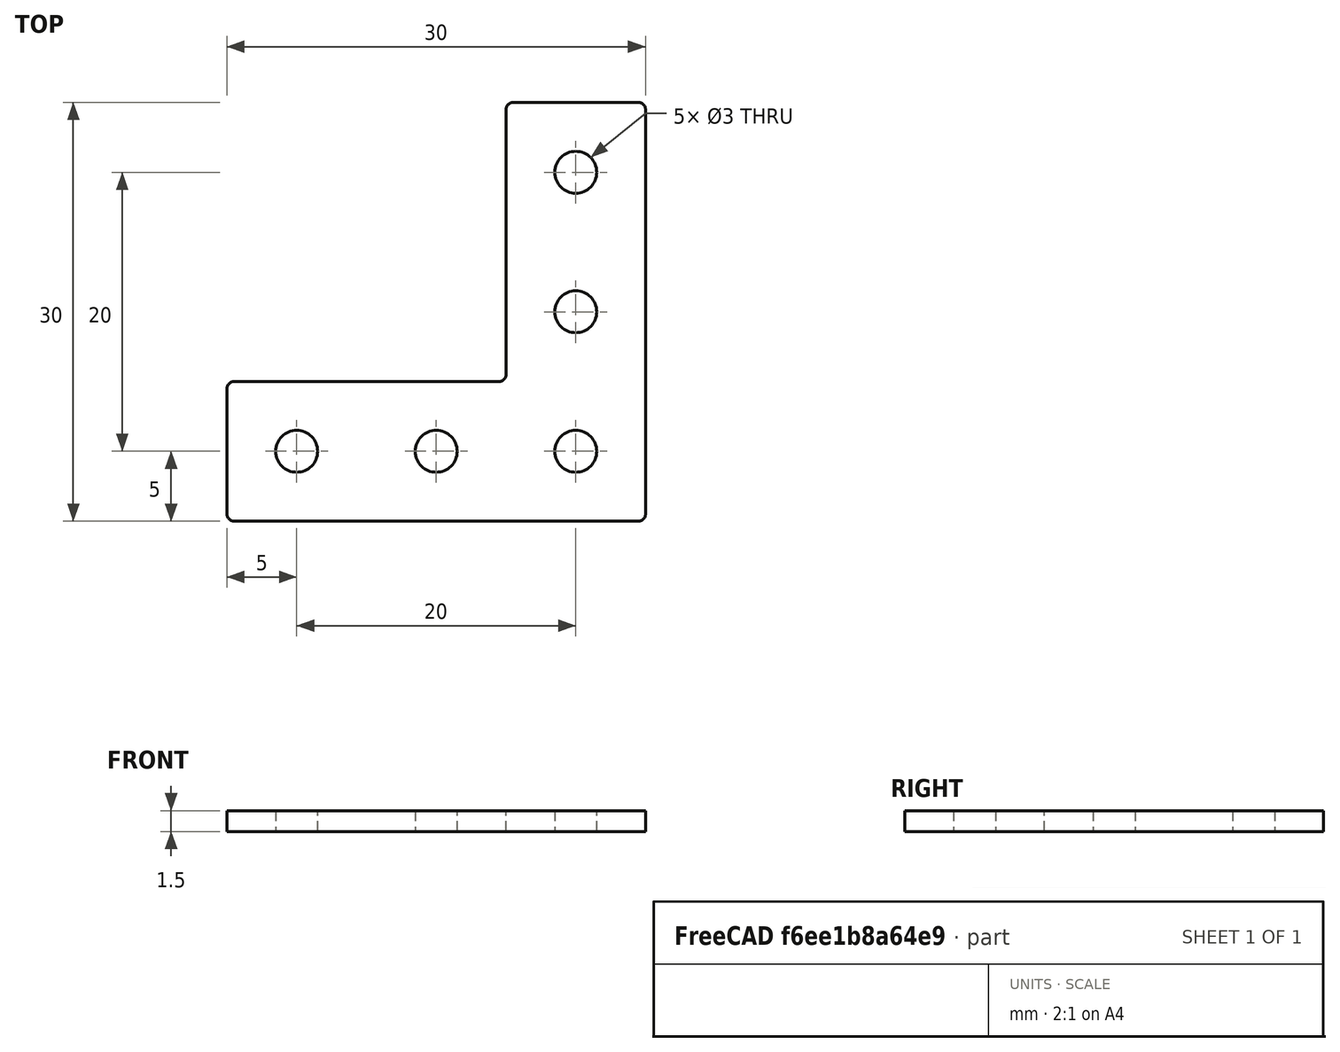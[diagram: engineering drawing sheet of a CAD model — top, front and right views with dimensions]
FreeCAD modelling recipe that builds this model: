
FCSTD DOCUMENT  (FreeCAD 0.18R16146 (Git))
Label: makerbeam_bracket_rightangle
License: All rights reserved
LicenseURL: http://en.wikipedia.org/wiki/All_rights_reserved
objects: Sketcher::SketchObject×1, PartDesign::Pad×1, PartDesign::Fillet×1, PartDesign::Body×1
note: 5 computed .brp shape members not serialized (recipe doc carries the construction recipe); baked Part::Feature solids carry a one-line shape summary decoded from their .brp

FEATURE [Sketcher::SketchObject] Sketch
  MapMode = 5
  Support = -> [XY_Plane]
  sketch-geometry (11):
    g0: Circle CenterX=-20 CenterY=0 CenterZ=0 NormalX=0 NormalY=0 NormalZ=1 AngleXU=0 Radius=1.5
    g1: Circle CenterX=-10 CenterY=0 CenterZ=0 NormalX=0 NormalY=0 NormalZ=1 AngleXU=0 Radius=1.5
    g2: Circle CenterX=0 CenterY=0 CenterZ=0 NormalX=0 NormalY=0 NormalZ=1 AngleXU=0 Radius=1.5
    g3: Circle CenterX=0 CenterY=10 CenterZ=0 NormalX=0 NormalY=0 NormalZ=1 AngleXU=0 Radius=1.5
    g4: LineSegment StartX=-25 StartY=-5 StartZ=0 EndX=5 EndY=-5 EndZ=0
    g5: LineSegment StartX=5 StartY=-5 StartZ=0 EndX=5 EndY=25 EndZ=0
    g6: LineSegment StartX=5 StartY=25 StartZ=0 EndX=-5 EndY=25 EndZ=0
    g7: LineSegment StartX=-5 StartY=25 StartZ=0 EndX=-5 EndY=5 EndZ=0
    g8: LineSegment StartX=-5 StartY=5 StartZ=0 EndX=-25 EndY=5 EndZ=0
    g9: LineSegment StartX=-25 StartY=5 StartZ=0 EndX=-25 EndY=-5 EndZ=0
    g10: Circle CenterX=0 CenterY=20 CenterZ=0 NormalX=0 NormalY=0 NormalZ=1 AngleXU=0 Radius=1.5
  constraints (17):
    c: Radius(g0) = 1.5
    c: Equal(g0,g1) = 1.5
    c: Equal(g0,g2) = 1.5
    c: Equal(g0,g3) = 1.5
    c: Horizontal(g4)
    c: Coincident(g4,g5)
    c: Vertical(g5)
    c: Coincident(g5,g6)
    c: Horizontal(g6)
    c: Coincident(g6,g7)
    c: Vertical(g7)
    c: Coincident(g7,g8)
    c: Horizontal(g8)
    c: Coincident(g8,g9)
    c: Coincident(g9,g4)
    c: Vertical(g9)
    c: PointOnObject(g10,g-2)
FEATURE [PartDesign::Pad] Pad
  Length = 1.5
  Length2 = 100
  Profile = -> Sketch
  Type = 0
FEATURE [PartDesign::Fillet] Fillet
  Base = -> Pad [Edge2,Edge14,Edge5,Edge8,Edge11,Edge1]
  BaseFeature = -> Pad
  Radius = 0.5
FEATURE [PartDesign::Body] Body  label="makerbeam_bracket_corner"
  Group = -> [Sketch,Pad,Fillet]
  Origin = -> Origin
  Tip = -> Fillet
